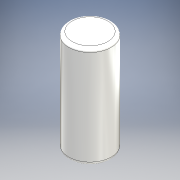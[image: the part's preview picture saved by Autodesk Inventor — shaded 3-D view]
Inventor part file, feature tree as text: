
AUTODESK INVENTOR PART (.ipt)
format: ipt  version: 2016 (Build 200138000, 138)  size: 109,568 bytes
history: native  units: mm
features: other x1, extrude x1, fillet x1, sketch x1
ambient origin geometry x8: Origin, YZ Plane, XZ Plane, XY Plane, X Axis, Y Axis, Z Axis, Center Point
bodies: Body1 (feature_tree)
feature tree (4):
  other  "ソリッド1"
  extrude  "押し出し1"  Depth=2.5mm
  fillet  "フィレット1"  Radius=6.0mm
  sketch  "スケッチ1"
